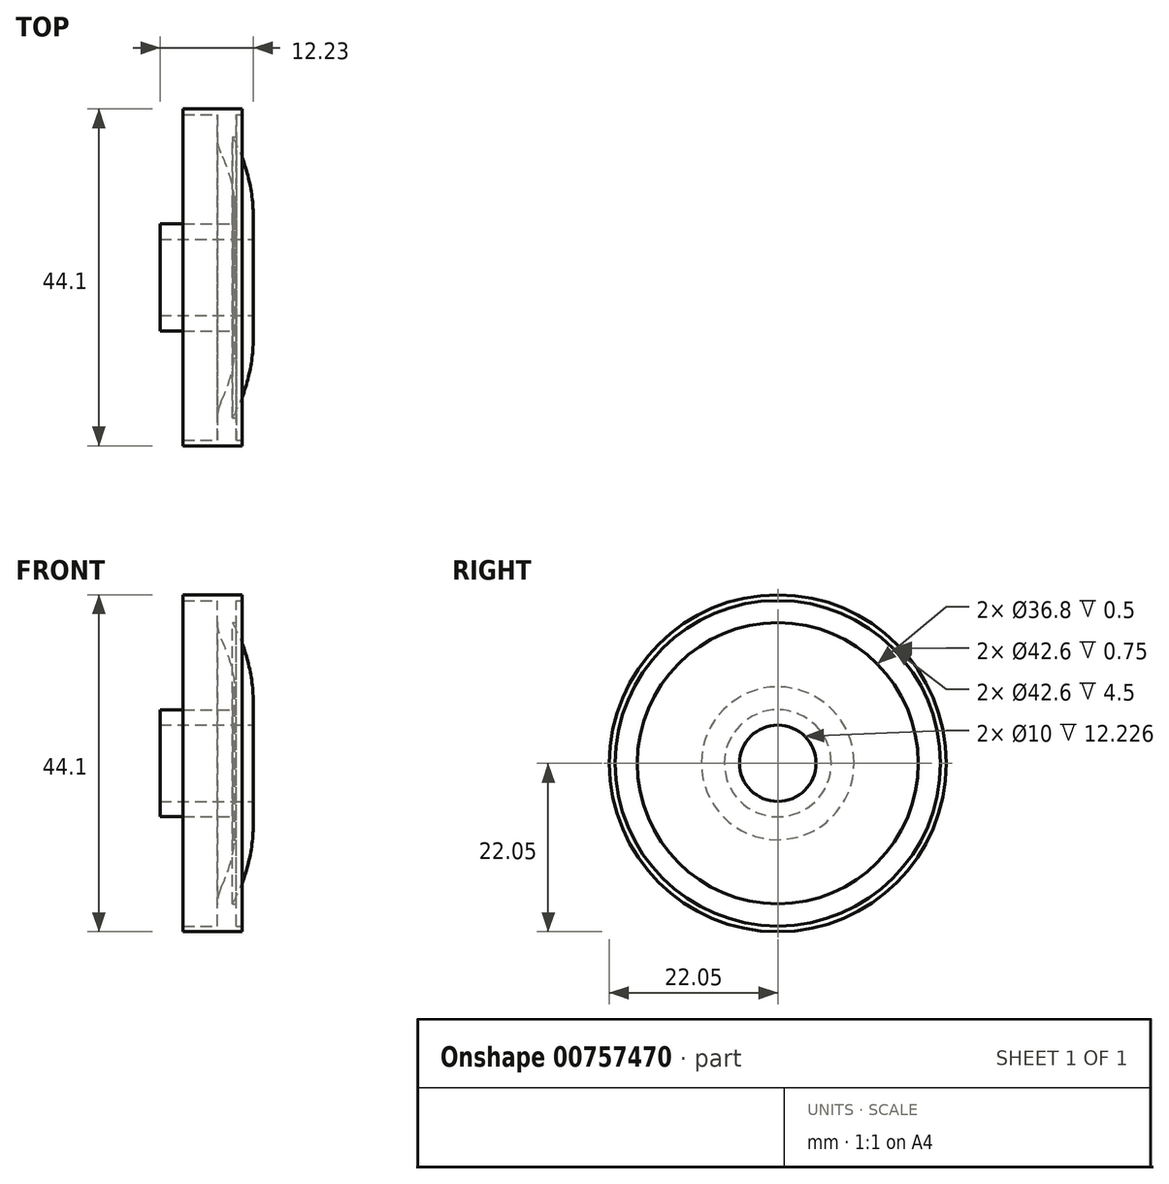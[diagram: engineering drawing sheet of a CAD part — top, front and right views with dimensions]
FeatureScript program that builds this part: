
annotation { "Feature Type Name" : "Feature", "Feature Type Description" : "" }
export const myFeature = defineFeature(function(context is Context, id is Id, definition is map)
    precondition{}
    {
        {
            var Q0;
            Q0=qCreatedBy(makeId("Front.planeOp"),FACE);
            var sketch = newSketch(context, id + "F0", { "sketchPlane" : qUnion([Q0])});
            skLineSegment(sketch, "E0", {"start": v(5.85, 0) * mm, "end": v(-6.86, 0) * mm});
            skLineSegment(sketch, "E1.0", {"start": v(3.87, 22.05) * mm, "end": v(-3.87, 22.05) * mm});
            skLineSegment(sketch, "E2.0", {"start": v(3.87, 21.3) * mm, "end": v(3.12, 21.3) * mm});
            skLineSegment(sketch, "E3.0", {"start": v(3.87, 22.05) * mm, "end": v(3.86, 21.3) * mm});
            skLineSegment(sketch, "E4.0", {"start": v(-3.86, 22.05) * mm, "end": v(-3.87, 21.3) * mm});
            skLineSegment(sketch, "E5.0", {"start": v(5.36, 5) * mm, "end": v(-6.86, 5) * mm});
            skLineSegment(sketch, "E6.0", {"start": v(-6.86, 7) * mm, "end": v(-6.86, 5) * mm});
            skLineSegment(sketch, "E7.0", {"start": v(2.7, 7) * mm, "end": v(-6.86, 7) * mm});
            skLineSegment(sketch, "E8.0", {"start": v(5.36, 7.72) * mm, "end": v(5.36, 5) * mm});
            skLineSegment(sketch, "E9", {"start": v(3.12, 21.3) * mm, "end": v(3.12, 18.4) * mm});
            skLineSegment(sketch, "E10.trimOffspring", {"start": v(0.63, 21.3) * mm, "end": v(-3.87, 21.3) * mm});
            skArc(sketch, "E11", {"start": v(5.36, 7.72) * mm, "mid": v(4.66, 13.23) * mm, "end": v(2.61, 18.4) * mm});
            skLineSegment(sketch, "E12.1", {"start": v(0.63, 21.3) * mm, "end": v(0.63, 17.27) * mm});
            skLineSegment(sketch, "E13", {"start": v(3.12, 18.4) * mm, "end": v(2.61, 18.4) * mm});
            skLineSegment(sketch, "E14", {"start": v(2.7, 7) * mm, "end": v(2.7, 10) * mm});
            skLineSegment(sketch, "E15", {"start": v(2.7, 10) * mm, "end": v(2.95, 10) * mm});
            skArc(sketch, "E16.0", {"start": v(2.95, 10) * mm, "mid": v(2.14, 13.75) * mm, "end": v(0.63, 17.27) * mm});
            skSolve(sketch);
        }
        {
            var Q0;
            Q0=makeQuery(id+"F0.imprint","IMPRINT",FACE,{"disambiguationData":[TD([[makeQuery(id+"F0.imprint","IMPRINT",EDGE,{"derivedFrom":sQuery(id+"F0.wireOp",EDGE,"E1.0")}),1.0]])]});
            var Q1;
            Q1=makeQuery(id+"F0.imprint","IMPRINT",FACE,{"disambiguationData":[TD([[makeQuery(id+"F0.imprint","IMPRINT",EDGE,{"derivedFrom":sQuery(id+"F0.wireOp",EDGE,"E5.0")}),-1.0]])]});
            var Q2;
            Q2=sQuery(id+"F0.wireOp",EDGE,"E0");
            revolve(context, id + "F1", {"surfaceOperationType" : NewSurfaceOperationType.NEW, "entities" : qUnion([Q0, Q1]), "axis" : qUnion([Q2]), "revolveType" : RevolveType.FULL});
        }
        {
            var Q0;
            Q0=makeQuery(id+"F1.opRevolve","SWEPT_EDGE",EDGE,{"disambiguationData":[OSD([sQuery(id+"F0.wireOp",EDGE,"E12.1"),sQuery(id+"F0.wireOp",EDGE,"E16.0")])]});
            fillet(context, id + "F2", {"entities" : qUnion([Q0]), "radius" : 5 * mm, "tangentPropagation" : true, "allowEdgeOverflow" : false});
        }
    });
